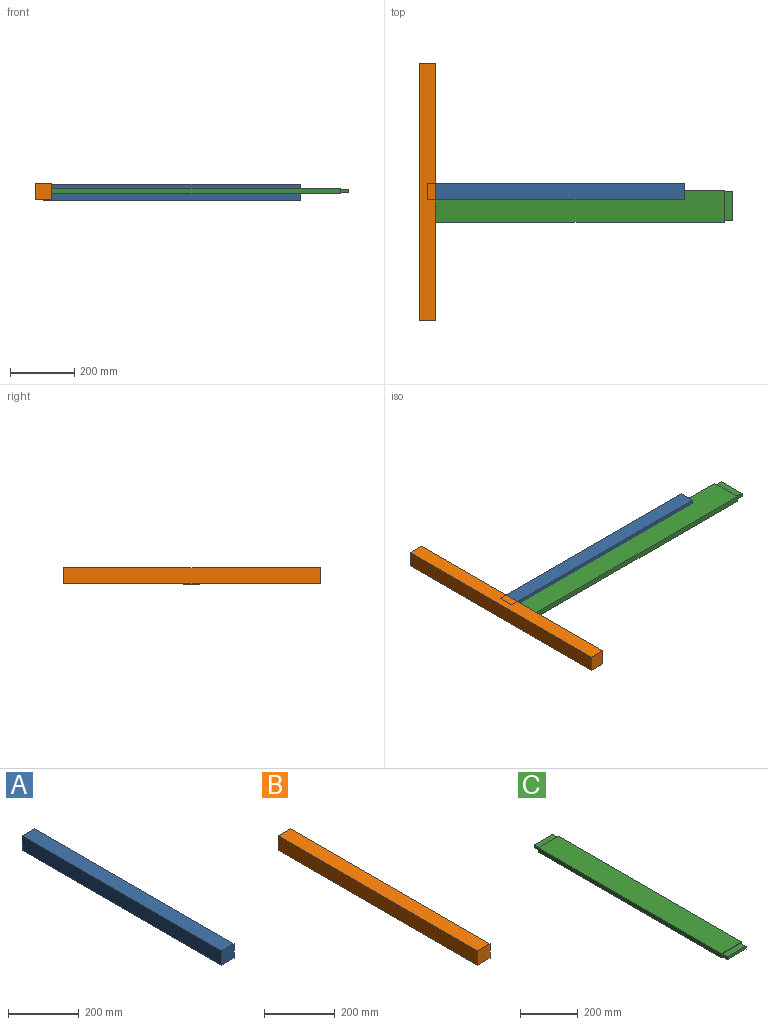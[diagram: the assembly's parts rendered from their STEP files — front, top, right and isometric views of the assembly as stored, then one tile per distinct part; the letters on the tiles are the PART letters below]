
ASSEMBLY  parts=3 mates=3
PART A: 11 faces, bbox 50x800x50 mm
  f0: plane 800x50mm, normal (1,0,0), area 38920mm2, adj f1,f3,f4,f5,f6,f7,f8,f9
  f1: plane 800x50mm, normal (0,0,1), area 40000mm2, adj f0,f2,f4,f5
  f2: plane 800x50mm, normal (-1,0,0), area 40000mm2, adj f1,f3,f4,f5
  f3: plane 800x50mm, normal (0,0,-1), area 40000mm2, adj f0,f2,f4,f5
  f4: plane 50x50mm, normal (0,-1,0), area 2500mm2, adj f0,f1,f2,f3
  f5: plane 50x50mm, normal (0,1,0), area 2500mm2, adj f0,f1,f2,f3
  f6: plane 90x25mm, normal (0,0,-1), area 2250mm2, adj f0,f7,f9,f10
  f7: plane 25x12mm, normal (0,1,0), area 300mm2, adj f0,f6,f8,f10
  f8: plane 90x25mm, normal (0,0,1), area 2250mm2, adj f0,f7,f9,f10
  f9: plane 25x12mm, normal (0,-1,0), area 300mm2, adj f0,f6,f8,f10
  f10: plane 90x12mm, normal (1,0,0), area 1080mm2, adj f6,f7,f8,f9
PART B: 11 faces, bbox 50x800x50 mm
  f0: plane 800x50mm, normal (1,0,0), area 38920mm2, adj f1,f3,f4,f5,f6,f7,f8,f9
  f1: plane 800x50mm, normal (0,0,1), area 40000mm2, adj f0,f2,f4,f5
  f2: plane 800x50mm, normal (-1,0,0), area 40000mm2, adj f1,f3,f4,f5
  f3: plane 800x50mm, normal (0,0,-1), area 40000mm2, adj f0,f2,f4,f5
  f4: plane 50x50mm, normal (0,-1,0), area 2500mm2, adj f0,f1,f2,f3
  f5: plane 50x50mm, normal (0,1,0), area 2500mm2, adj f0,f1,f2,f3
  f6: plane 90x25mm, normal (0,0,-1), area 2250mm2, adj f0,f7,f9,f10
  f7: plane 25x12mm, normal (0,1,0), area 300mm2, adj f0,f6,f8,f10
  f8: plane 90x25mm, normal (0,0,1), area 2250mm2, adj f0,f7,f9,f10
  f9: plane 25x12mm, normal (0,-1,0), area 300mm2, adj f0,f6,f8,f10
  f10: plane 90x12mm, normal (1,0,0), area 1080mm2, adj f6,f7,f8,f9
PART C: 16 faces, bbox 100x950x18 mm
  f0: plane 100x18mm, normal (0,1,0), area 720mm2, adj f1,f2,f3,f4,f11,f12,f13,f14
  f1: plane 900x100mm, normal (0,0,1), area 90000mm2, adj f0,f2,f4,f5
  f2: plane 900x18mm, normal (-1,0,0), area 16200mm2, adj f0,f1,f3,f5
  f3: plane 900x100mm, normal (0,0,-1), area 90000mm2, adj f0,f2,f4,f5
  f4: plane 900x18mm, normal (1,0,0), area 16200mm2, adj f0,f1,f3,f5
  f5: plane 100x18mm, normal (0,-1,0), area 720mm2, adj f1,f2,f3,f4,f6,f7,f8,f9
  f6: plane 25x12mm, normal (-1,0,0), area 300mm2, adj f5,f7,f9,f10
  f7: plane 90x25mm, normal (0,0,-1), area 2250mm2, adj f5,f6,f8,f10
  f8: plane 25x12mm, normal (1,0,0), area 300mm2, adj f5,f7,f9,f10
  f9: plane 90x25mm, normal (0,0,1), area 2250mm2, adj f5,f6,f8,f10
  f10: plane 90x12mm, normal (0,-1,0), area 1080mm2, adj f6,f7,f8,f9
  f11: plane 25x12mm, normal (1,0,0), area 300mm2, adj f0,f12,f14,f15
  f12: plane 90x25mm, normal (0,0,-1), area 2250mm2, adj f0,f11,f13,f15
  f13: plane 25x12mm, normal (-1,0,0), area 300mm2, adj f0,f12,f14,f15
  f14: plane 90x25mm, normal (0,0,1), area 2250mm2, adj f0,f11,f13,f15
  f15: plane 90x12mm, normal (0,1,0), area 1080mm2, adj f11,f12,f13,f14
PLACE A rot(axis=(0.58,0.58,-0.58),120deg) t=(825,-352.5,141.83)mm
PLACE B t=(25,46.25,41.92)mm
PLACE C rot(axis=(-0.71,-0.71,0),180deg) t=(950,-398.75,44.92)mm
MATE parallel C.f7 <-> B.f6  axis (0,0,1) through (37.5,-398.75,50.92)mm
MATE slider A.f4 <-> B.f0  axis (-1,0,0) through (25,-352.5,41.83)mm
MATE parallel B.f10 <-> C.f10  axis (1,0,0) through (25,-398.75,44.92)mm
